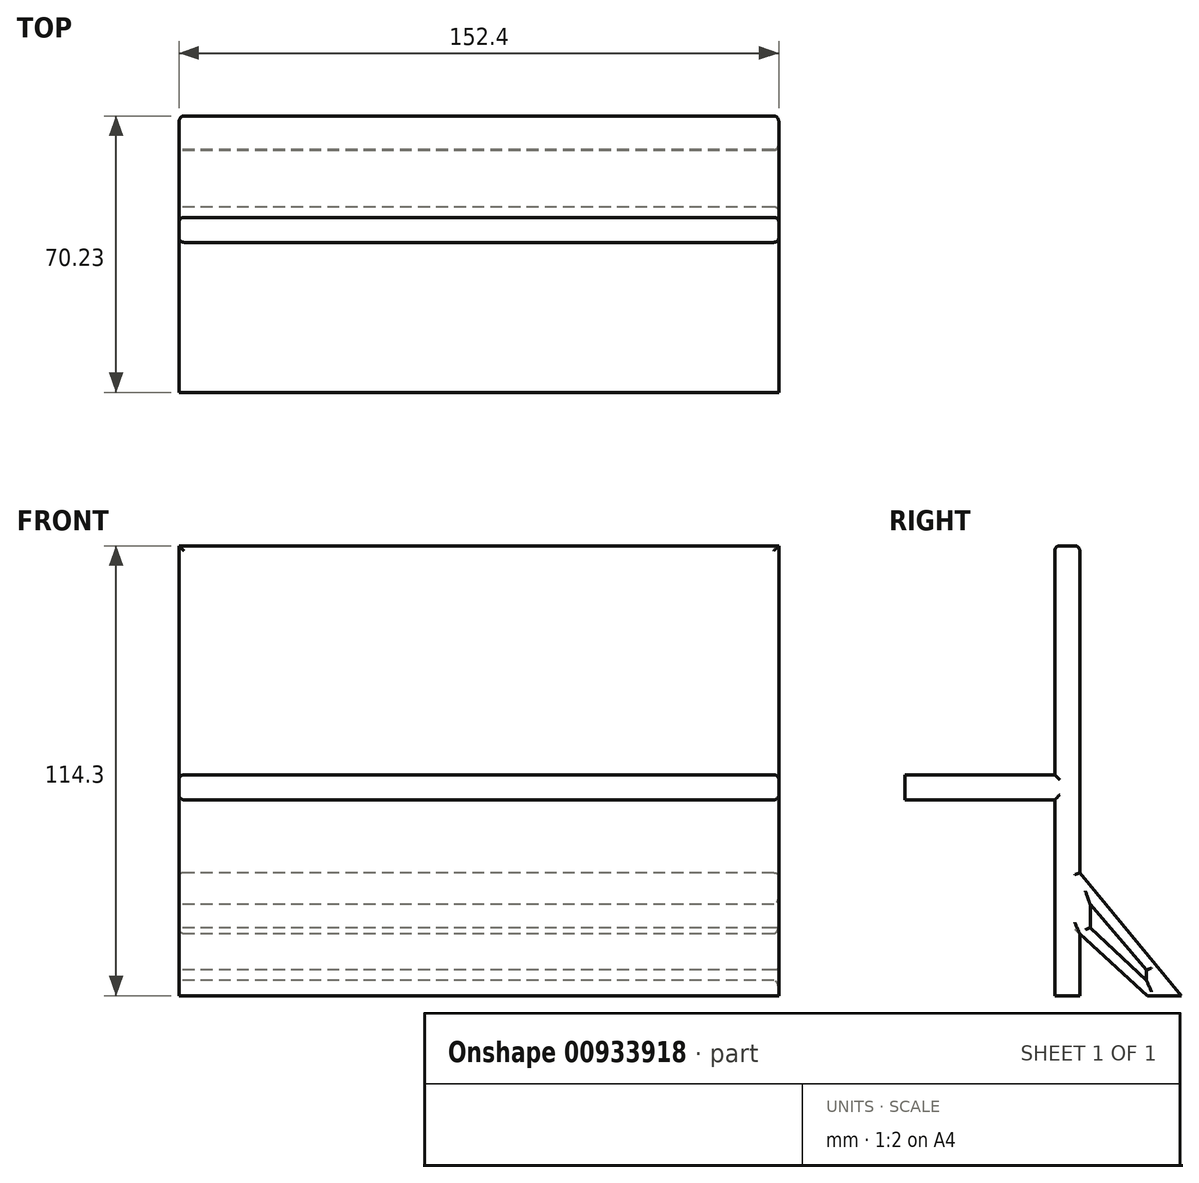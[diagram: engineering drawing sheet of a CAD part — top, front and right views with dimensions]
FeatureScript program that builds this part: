
annotation { "Feature Type Name" : "Feature", "Feature Type Description" : "" }
export const myFeature = defineFeature(function(context is Context, id is Id, definition is map)
    precondition{}
    {
        {
            var Q0;
            Q0=qCreatedBy(makeId("Right.planeOp"),FACE);
            var sketch = newSketch(context, id + "F0", { "sketchPlane" : qUnion([Q0])});
            skLineSegment(sketch, "E0", {"start": v(25.4, -45.43) * mm, "end": v(25.4, 68.87) * mm});
            skLineSegment(sketch, "E1", {"start": v(25.4, 68.87) * mm, "end": v(19.05, 68.87) * mm});
            skLineSegment(sketch, "E2", {"start": v(19.05, 68.87) * mm, "end": v(19.05, -45.43) * mm});
            skLineSegment(sketch, "E3", {"start": v(19.05, -45.43) * mm, "end": v(25.4, -45.43) * mm});
            skLineSegment(sketch, "E4", {"start": v(25.4, -45.43) * mm, "end": v(66.93, -45.43) * mm, "construction": true});
            skLineSegment(sketch, "E5", {"start": v(51.18, -45.43) * mm, "end": v(25.4, -14.25) * mm});
            skLineSegment(sketch, "E6", {"start": v(25.4, -14.25) * mm, "end": v(25.4, -29.7) * mm});
            skLineSegment(sketch, "E7", {"start": v(25.4, -29.7) * mm, "end": v(42.58, -45.43) * mm});
            skLineSegment(sketch, "E8", {"start": v(42.58, -45.43) * mm, "end": v(51.18, -45.43) * mm});
            skLineSegment(sketch, "E9", {"start": v(28.05, -22.21) * mm, "end": v(28.05, -28.15) * mm});
            skLineSegment(sketch, "E10", {"start": v(28.05, -28.15) * mm, "end": v(42.37, -41.55) * mm});
            skLineSegment(sketch, "E11", {"start": v(42.37, -41.55) * mm, "end": v(42.37, -38.9) * mm});
            skLineSegment(sketch, "E12", {"start": v(42.37, -38.9) * mm, "end": v(28.05, -22.21) * mm});
            skSolve(sketch);
        }
        {
            var Q0;
            Q0=qCreatedBy(makeId("Right.planeOp"),FACE);
            var sketch = newSketch(context, id + "F1", { "sketchPlane" : qUnion([Q0])});
            skLineSegment(sketch, "E13.0", {"start": v(19.05, 68.87) * mm, "end": v(19.05, -45.43) * mm});
            skLineSegment(sketch, "E14.0", {"start": v(-19.05, 68.87) * mm, "end": v(-19.05, -45.43) * mm});
            skLineSegment(sketch, "E15", {"start": v(0, -46.47) * mm, "end": v(0, 4.33) * mm, "construction": true});
            skLineSegment(sketch, "E16", {"start": v(19.05, 4.33) * mm, "end": v(-19.05, 4.33) * mm});
            skLineSegment(sketch, "E17", {"start": v(-19.05, 4.33) * mm, "end": v(-19.05, 10.68) * mm});
            skLineSegment(sketch, "E18", {"start": v(-19.05, 10.68) * mm, "end": v(19.05, 10.68) * mm});
            skPoint(sketch, "E18.endSnap0", {"position": v(19.05, 11.72) * mm});
            skLineSegment(sketch, "E19", {"start": v(19.05, 10.68) * mm, "end": v(19.05, 4.33) * mm});
            skSolve(sketch);
        }
        {
            var Q0;
            Q0=makeQuery(id+"F0.imprint","IMPRINT",FACE,{"disambiguationData":[TD([[makeQuery(id+"F0.imprint","IMPRINT",EDGE,{"derivedFrom":sQuery(id+"F0.wireOp",EDGE,"E5")}),1.0]])]});
            var Q1;
            Q1=makeQuery(id+"F0.imprint","IMPRINT",FACE,{"disambiguationData":[TD([[makeQuery(id+"F0.imprint","IMPRINT",EDGE,{"derivedFrom":sQuery(id+"F0.wireOp",EDGE,"E9")}),1.0]])]});
            var Q2;
            {var subQ0=sQuery(id+"F0.wireOp",EDGE,"E1");Q2=makeQuery(id+"F0.imprint","IMPRINT",FACE,{"disambiguationData":[TD([[makeQuery(id+"F0.imprint","IMPRINT",EDGE,{"derivedFrom":subQ0}),1.0]])]});}
            var Q3;
            Q3=makeQuery(id+"F1.imprint","IMPRINT",FACE,{"disambiguationData":[TD([[makeQuery(id+"F1.imprint","IMPRINT",EDGE,{"derivedFrom":sQuery(id+"F1.wireOp",EDGE,"E16")}),-1.0]])]});
            var Q4;
            {var subQ0=sQuery(id+"Fzd2bILkkweZFFx_0.1.F0.wireOp",EDGE,"E1");Q4=makeQuery(id+"Fzd2bILkkweZFFx_0.1.F0.imprint","IMPRINT",FACE,{"disambiguationData":[TD([[makeQuery(id+"Fzd2bILkkweZFFx_0.1.F0.imprint","IMPRINT",EDGE,{"derivedFrom":subQ0}),1.0]])]});}
            var Q5;
            Q5=makeQuery(id+"Fzd2bILkkweZFFx_0.1.F0.imprint","IMPRINT",FACE,{"disambiguationData":[TD([[makeQuery(id+"Fzd2bILkkweZFFx_0.1.F0.imprint","IMPRINT",EDGE,{"derivedFrom":sQuery(id+"Fzd2bILkkweZFFx_0.1.F0.wireOp",EDGE,"E5")}),1.0]])]});
            var Q6;
            Q6=makeQuery(id+"Fzd2bILkkweZFFx_0.1.F0.imprint","IMPRINT",FACE,{"disambiguationData":[TD([[makeQuery(id+"Fzd2bILkkweZFFx_0.1.F0.imprint","IMPRINT",EDGE,{"derivedFrom":sQuery(id+"Fzd2bILkkweZFFx_0.1.F0.wireOp",EDGE,"E9")}),1.0]])]});
            extrude(context, id + "F2", {"entities" : qUnion([Q0, Q1, Q2, Q3, Q4, Q5, Q6]), "depth" : 152.4 * mm, "offsetDistance" : 25.4 * mm});
        }
        {
            var Q0;
            Q0=makeQuery(id+"F0.imprint","IMPRINT",FACE,{"disambiguationData":[TD([[makeQuery(id+"F0.imprint","IMPRINT",EDGE,{"derivedFrom":sQuery(id+"F0.wireOp",EDGE,"E9")}),1.0]])]});
            var Q1;
            Q1=makeQuery(id+"Fzd2bILkkweZFFx_0.1.F0.imprint","IMPRINT",FACE,{"disambiguationData":[TD([[makeQuery(id+"Fzd2bILkkweZFFx_0.1.F0.imprint","IMPRINT",EDGE,{"derivedFrom":sQuery(id+"Fzd2bILkkweZFFx_0.1.F0.wireOp",EDGE,"E9")}),1.0]])]});
            extrude(context, id + "F3", {"entities" : qUnion([Q0, Q1]), "operationType" : NewBodyOperationType.REMOVE, "depth" : 157.48 * mm, "offsetDistance" : 25.4 * mm});
        }
        {
            var Q0;
            Q0=makeQuery(id+"F2.opExtrude","SWEPT_BODY",BODY,{"disambiguationData":[OSD([sQuery(id+"F0.wireOp",EDGE,"E0"),sQuery(id+"F0.wireOp",EDGE,"E1"),sQuery(id+"F0.wireOp",EDGE,"E2"),sQuery(id+"F0.wireOp",EDGE,"E3"),sQuery(id+"F0.wireOp",EDGE,"E5"),sQuery(id+"F0.wireOp",EDGE,"E7"),sQuery(id+"F0.wireOp",EDGE,"E8")])]});
            var Q1;
            Q1=makeQuery(id+"F2.opExtrude","SWEPT_BODY",BODY,{"disambiguationData":[OSD([sQuery(id+"Fzd2bILkkweZFFx_0.1.F0.wireOp",EDGE,"E0"),sQuery(id+"Fzd2bILkkweZFFx_0.1.F0.wireOp",EDGE,"E1"),sQuery(id+"Fzd2bILkkweZFFx_0.1.F0.wireOp",EDGE,"E2"),sQuery(id+"Fzd2bILkkweZFFx_0.1.F0.wireOp",EDGE,"E3"),sQuery(id+"Fzd2bILkkweZFFx_0.1.F0.wireOp",EDGE,"E5"),sQuery(id+"Fzd2bILkkweZFFx_0.1.F0.wireOp",EDGE,"E7"),sQuery(id+"Fzd2bILkkweZFFx_0.1.F0.wireOp",EDGE,"E8")])]});
            var Q2;
            Q2=makeQuery(id+"F2.opExtrude","SWEPT_BODY",BODY,{"disambiguationData":[OSD([sQuery(id+"F1.wireOp",EDGE,"E16"),sQuery(id+"F1.wireOp",EDGE,"E17"),sQuery(id+"F1.wireOp",EDGE,"E18"),sQuery(id+"F1.wireOp",EDGE,"E19")])]});
            booleanBodies(context, id + "F4", {"operationType" : BooleanOperationType.UNION, "tools" : qUnion([Q0, Q1, Q2])});
        }
        {
            var Q0;
            Q0=makeQuery(id+"F2.opExtrude","SWEPT_EDGE",EDGE,{"disambiguationData":[OSD([sQuery(id+"Fzd2bILkkweZFFx_0.1.F0.wireOp",EDGE,"E1"),sQuery(id+"Fzd2bILkkweZFFx_0.1.F0.wireOp",EDGE,"E2")])]});
            var Q1;
            Q1=makeQuery(id+"F2.opExtrude","SWEPT_EDGE",EDGE,{"disambiguationData":[OSD([sQuery(id+"F0.wireOp",EDGE,"E1"),sQuery(id+"F0.wireOp",EDGE,"E2")])]});
            var Q2;
            {var subQ0=sQuery(id+"Fzd2bILkkweZFFx_0.1.F0.wireOp",EDGE,"E2");var subQ1=sQuery(id+"Fzd2bILkkweZFFx_0.1.F0.wireOp",EDGE,"E1");Q2=makeQuery(id+"F4.opBoolean","SPLIT",EDGE,{"disambiguationData":[TD([makeQuery(id+"F2.opExtrude","SWEPT_FACE",FACE,{"disambiguationData":[OSD([subQ1])]})])],"derivedFrom":makeQuery(id+"F2.opExtrude","CAP_EDGE",EDGE,{"disambiguationData":[OSD([subQ0])],"isStart":false})});}
            var Q3;
            {var subQ0=sQuery(id+"F0.wireOp",EDGE,"E2");var subQ1=sQuery(id+"F0.wireOp",EDGE,"E1");Q3=makeQuery(id+"F4.opBoolean","SPLIT",EDGE,{"disambiguationData":[TD([makeQuery(id+"F2.opExtrude","SWEPT_FACE",FACE,{"disambiguationData":[OSD([subQ1])]})])],"derivedFrom":makeQuery(id+"F2.opExtrude","CAP_EDGE",EDGE,{"disambiguationData":[OSD([subQ0])],"isStart":false})});}
            var Q4;
            {var subQ0=sQuery(id+"Fzd2bILkkweZFFx_0.1.F0.wireOp",EDGE,"E3");var subQ1=sQuery(id+"Fzd2bILkkweZFFx_0.1.F0.wireOp",EDGE,"E2");Q4=makeQuery(id+"F4.opBoolean","SPLIT",EDGE,{"disambiguationData":[TD([makeQuery(id+"F2.opExtrude","SWEPT_FACE",FACE,{"disambiguationData":[OSD([subQ0])]})])],"derivedFrom":makeQuery(id+"F2.opExtrude","CAP_EDGE",EDGE,{"disambiguationData":[OSD([subQ1])],"isStart":false})});}
            var Q5;
            {var subQ0=sQuery(id+"F0.wireOp",EDGE,"E3");var subQ1=sQuery(id+"F0.wireOp",EDGE,"E2");Q5=makeQuery(id+"F4.opBoolean","SPLIT",EDGE,{"disambiguationData":[TD([makeQuery(id+"F2.opExtrude","SWEPT_FACE",FACE,{"disambiguationData":[OSD([subQ0])]})])],"derivedFrom":makeQuery(id+"F2.opExtrude","CAP_EDGE",EDGE,{"disambiguationData":[OSD([subQ1])],"isStart":false})});}
            var Q6;
            Q6=makeQuery(id+"F2.opExtrude","CAP_EDGE",EDGE,{"disambiguationData":[OSD([sQuery(id+"F1.wireOp",EDGE,"E16")])],"isStart":false});
            var Q7;
            Q7=makeQuery(id+"F2.opExtrude","CAP_EDGE",EDGE,{"disambiguationData":[OSD([sQuery(id+"F1.wireOp",EDGE,"E18")])],"isStart":false});
            var Q8;
            Q8=makeQuery(id+"F2.opExtrude","CAP_EDGE",EDGE,{"disambiguationData":[OSD([sQuery(id+"F1.wireOp",EDGE,"E18")])],"isStart":true});
            var Q9;
            Q9=makeQuery(id+"F2.opExtrude","CAP_EDGE",EDGE,{"disambiguationData":[OSD([sQuery(id+"F1.wireOp",EDGE,"E16")])],"isStart":true});
            var Q10;
            {var subQ0=sQuery(id+"F0.wireOp",EDGE,"E2");var subQ1=sQuery(id+"F0.wireOp",EDGE,"E1");Q10=makeQuery(id+"F4.opBoolean","SPLIT",EDGE,{"disambiguationData":[TD([makeQuery(id+"F2.opExtrude","SWEPT_FACE",FACE,{"disambiguationData":[OSD([subQ1])]})])],"derivedFrom":makeQuery(id+"F2.opExtrude","CAP_EDGE",EDGE,{"disambiguationData":[OSD([subQ0])],"isStart":true})});}
            var Q11;
            {var subQ0=sQuery(id+"F0.wireOp",EDGE,"E2");var subQ1=sQuery(id+"F0.wireOp",EDGE,"E3");Q11=makeQuery(id+"F4.opBoolean","SPLIT",EDGE,{"disambiguationData":[TD([makeQuery(id+"F2.opExtrude","SWEPT_FACE",FACE,{"disambiguationData":[OSD([subQ1])]})])],"derivedFrom":makeQuery(id+"F2.opExtrude","CAP_EDGE",EDGE,{"disambiguationData":[OSD([subQ0])],"isStart":true})});}
            var Q12;
            {var subQ0=sQuery(id+"Fzd2bILkkweZFFx_0.1.F0.wireOp",EDGE,"E2");var subQ1=sQuery(id+"Fzd2bILkkweZFFx_0.1.F0.wireOp",EDGE,"E3");Q12=makeQuery(id+"F4.opBoolean","SPLIT",EDGE,{"disambiguationData":[TD([makeQuery(id+"F2.opExtrude","SWEPT_FACE",FACE,{"disambiguationData":[OSD([subQ1])]})])],"derivedFrom":makeQuery(id+"F2.opExtrude","CAP_EDGE",EDGE,{"disambiguationData":[OSD([subQ0])],"isStart":true})});}
            var Q13;
            {var subQ0=sQuery(id+"Fzd2bILkkweZFFx_0.1.F0.wireOp",EDGE,"E2");var subQ1=sQuery(id+"Fzd2bILkkweZFFx_0.1.F0.wireOp",EDGE,"E1");Q13=makeQuery(id+"F4.opBoolean","SPLIT",EDGE,{"disambiguationData":[TD([makeQuery(id+"F2.opExtrude","SWEPT_FACE",FACE,{"disambiguationData":[OSD([subQ1])]})])],"derivedFrom":makeQuery(id+"F2.opExtrude","CAP_EDGE",EDGE,{"disambiguationData":[OSD([subQ0])],"isStart":true})});}
            var Q14;
            Q14=makeQuery(id+"F2.opExtrude","SWEPT_EDGE",EDGE,{"disambiguationData":[OSD([sQuery(id+"Fzd2bILkkweZFFx_0.1.F0.wireOp",EDGE,"E0"),sQuery(id+"Fzd2bILkkweZFFx_0.1.F0.wireOp",EDGE,"E1")])]});
            var Q15;
            {var subQ0=sQuery(id+"Fzd2bILkkweZFFx_0.1.F0.wireOp",EDGE,"E0");Q15=makeQuery(id+"F2.opExtrude","CAP_EDGE",EDGE,{"disambiguationData":[OSD([subQ0]),TDD([makeQuery(id+"Fzd2bILkkweZFFx_0.1.F0.imprint","IMPRINT",EDGE,{"disambiguationData":[TD([[makeQuery(id+"Fzd2bILkkweZFFx_0.1.F0.imprint","INTERSECT",VERTEX,{"derivedFrom":[subQ0,sQuery(id+"Fzd2bILkkweZFFx_0.1.F0.wireOp",EDGE,"E1")]}),1.0]])],"derivedFrom":subQ0})])],"isStart":false});}
            var Q16;
            {var subQ0=sQuery(id+"Fzd2bILkkweZFFx_0.1.F0.wireOp",EDGE,"E0");Q16=makeQuery(id+"F2.opExtrude","CAP_EDGE",EDGE,{"disambiguationData":[OSD([subQ0]),TDD([makeQuery(id+"Fzd2bILkkweZFFx_0.1.F0.imprint","IMPRINT",EDGE,{"disambiguationData":[TD([[makeQuery(id+"Fzd2bILkkweZFFx_0.1.F0.imprint","INTERSECT",VERTEX,{"derivedFrom":[subQ0,sQuery(id+"Fzd2bILkkweZFFx_0.1.F0.wireOp",EDGE,"E1")]}),1.0]])],"derivedFrom":subQ0})])],"isStart":true});}
            var Q17;
            {var subQ0=sQuery(id+"F0.wireOp",EDGE,"E0");Q17=makeQuery(id+"F2.opExtrude","CAP_EDGE",EDGE,{"disambiguationData":[OSD([subQ0]),TDD([makeQuery(id+"F0.imprint","IMPRINT",EDGE,{"disambiguationData":[TD([[makeQuery(id+"F0.imprint","INTERSECT",VERTEX,{"derivedFrom":[subQ0,sQuery(id+"F0.wireOp",EDGE,"E1")]}),1.0]])],"derivedFrom":subQ0})])],"isStart":true});}
            var Q18;
            Q18=makeQuery(id+"F2.opExtrude","SWEPT_EDGE",EDGE,{"disambiguationData":[OSD([sQuery(id+"F0.wireOp",EDGE,"E0"),sQuery(id+"F0.wireOp",EDGE,"E1")])]});
            var Q19;
            {var subQ0=sQuery(id+"F0.wireOp",EDGE,"E0");Q19=makeQuery(id+"F2.opExtrude","CAP_EDGE",EDGE,{"disambiguationData":[OSD([subQ0]),TDD([makeQuery(id+"F0.imprint","IMPRINT",EDGE,{"disambiguationData":[TD([[makeQuery(id+"F0.imprint","INTERSECT",VERTEX,{"derivedFrom":[subQ0,sQuery(id+"F0.wireOp",EDGE,"E1")]}),1.0]])],"derivedFrom":subQ0})])],"isStart":false});}
            fillet(context, id + "F5", {"entities" : qUnion([Q0, Q1, Q2, Q3, Q4, Q5, Q6, Q7, Q8, Q9, Q10, Q11, Q12, Q13, Q14, Q15, Q16, Q17, Q18, Q19]), "radius" : 1.27 * mm, "tangentPropagation" : true, "allowEdgeOverflow" : false});
        }
        {
            var Q0;
            Q0=makeQuery(id+"F3.boolean.opBoolean","INTERSECT",EDGE,{"derivedFrom":[makeQuery(id+"F2.opExtrude","CAP_FACE",FACE,{"disambiguationData":[OSD([sQuery(id+"Fzd2bILkkweZFFx_0.1.F0.wireOp",EDGE,"E0"),sQuery(id+"Fzd2bILkkweZFFx_0.1.F0.wireOp",EDGE,"E1"),sQuery(id+"Fzd2bILkkweZFFx_0.1.F0.wireOp",EDGE,"E2"),sQuery(id+"Fzd2bILkkweZFFx_0.1.F0.wireOp",EDGE,"E3"),sQuery(id+"Fzd2bILkkweZFFx_0.1.F0.wireOp",EDGE,"E5"),sQuery(id+"Fzd2bILkkweZFFx_0.1.F0.wireOp",EDGE,"E7"),sQuery(id+"Fzd2bILkkweZFFx_0.1.F0.wireOp",EDGE,"E8")])],"isStart":false}),makeQuery(id+"F3.opExtrude","SWEPT_FACE",FACE,{"disambiguationData":[OSD([sQuery(id+"Fzd2bILkkweZFFx_0.1.F0.wireOp",EDGE,"E12")])]})]});
            var Q1;
            Q1=makeQuery(id+"F3.boolean.opBoolean","INTERSECT",EDGE,{"derivedFrom":[makeQuery(id+"F2.opExtrude","CAP_FACE",FACE,{"disambiguationData":[OSD([sQuery(id+"Fzd2bILkkweZFFx_0.1.F0.wireOp",EDGE,"E0"),sQuery(id+"Fzd2bILkkweZFFx_0.1.F0.wireOp",EDGE,"E1"),sQuery(id+"Fzd2bILkkweZFFx_0.1.F0.wireOp",EDGE,"E2"),sQuery(id+"Fzd2bILkkweZFFx_0.1.F0.wireOp",EDGE,"E3"),sQuery(id+"Fzd2bILkkweZFFx_0.1.F0.wireOp",EDGE,"E5"),sQuery(id+"Fzd2bILkkweZFFx_0.1.F0.wireOp",EDGE,"E7"),sQuery(id+"Fzd2bILkkweZFFx_0.1.F0.wireOp",EDGE,"E8")])],"isStart":false}),makeQuery(id+"F3.opExtrude","SWEPT_FACE",FACE,{"disambiguationData":[OSD([sQuery(id+"Fzd2bILkkweZFFx_0.1.F0.wireOp",EDGE,"E10")])]})]});
            var Q2;
            Q2=makeQuery(id+"F3.boolean.opBoolean","INTERSECT",EDGE,{"derivedFrom":[makeQuery(id+"F2.opExtrude","CAP_FACE",FACE,{"disambiguationData":[OSD([sQuery(id+"Fzd2bILkkweZFFx_0.1.F0.wireOp",EDGE,"E0"),sQuery(id+"Fzd2bILkkweZFFx_0.1.F0.wireOp",EDGE,"E1"),sQuery(id+"Fzd2bILkkweZFFx_0.1.F0.wireOp",EDGE,"E2"),sQuery(id+"Fzd2bILkkweZFFx_0.1.F0.wireOp",EDGE,"E3"),sQuery(id+"Fzd2bILkkweZFFx_0.1.F0.wireOp",EDGE,"E5"),sQuery(id+"Fzd2bILkkweZFFx_0.1.F0.wireOp",EDGE,"E7"),sQuery(id+"Fzd2bILkkweZFFx_0.1.F0.wireOp",EDGE,"E8")])],"isStart":false}),makeQuery(id+"F3.opExtrude","SWEPT_FACE",FACE,{"disambiguationData":[OSD([sQuery(id+"Fzd2bILkkweZFFx_0.1.F0.wireOp",EDGE,"E9")])]})]});
            var Q3;
            Q3=makeQuery(id+"F3.boolean.opBoolean","INTERSECT",EDGE,{"derivedFrom":[makeQuery(id+"F2.opExtrude","CAP_FACE",FACE,{"disambiguationData":[OSD([sQuery(id+"Fzd2bILkkweZFFx_0.1.F0.wireOp",EDGE,"E0"),sQuery(id+"Fzd2bILkkweZFFx_0.1.F0.wireOp",EDGE,"E1"),sQuery(id+"Fzd2bILkkweZFFx_0.1.F0.wireOp",EDGE,"E2"),sQuery(id+"Fzd2bILkkweZFFx_0.1.F0.wireOp",EDGE,"E3"),sQuery(id+"Fzd2bILkkweZFFx_0.1.F0.wireOp",EDGE,"E5"),sQuery(id+"Fzd2bILkkweZFFx_0.1.F0.wireOp",EDGE,"E7"),sQuery(id+"Fzd2bILkkweZFFx_0.1.F0.wireOp",EDGE,"E8")])],"isStart":false}),makeQuery(id+"F3.opExtrude","SWEPT_FACE",FACE,{"disambiguationData":[OSD([sQuery(id+"Fzd2bILkkweZFFx_0.1.F0.wireOp",EDGE,"E11")])]})]});
            var Q4;
            Q4=makeQuery(id+"F3.boolean.opBoolean","INTERSECT",EDGE,{"derivedFrom":[makeQuery(id+"F2.opExtrude","CAP_FACE",FACE,{"disambiguationData":[OSD([sQuery(id+"F0.wireOp",EDGE,"E0"),sQuery(id+"F0.wireOp",EDGE,"E1"),sQuery(id+"F0.wireOp",EDGE,"E2"),sQuery(id+"F0.wireOp",EDGE,"E3"),sQuery(id+"F0.wireOp",EDGE,"E5"),sQuery(id+"F0.wireOp",EDGE,"E7"),sQuery(id+"F0.wireOp",EDGE,"E8")])],"isStart":false}),makeQuery(id+"F3.opExtrude","SWEPT_FACE",FACE,{"disambiguationData":[OSD([sQuery(id+"F0.wireOp",EDGE,"E10")])]})]});
            var Q5;
            Q5=makeQuery(id+"F3.boolean.opBoolean","INTERSECT",EDGE,{"derivedFrom":[makeQuery(id+"F2.opExtrude","CAP_FACE",FACE,{"disambiguationData":[OSD([sQuery(id+"F0.wireOp",EDGE,"E0"),sQuery(id+"F0.wireOp",EDGE,"E1"),sQuery(id+"F0.wireOp",EDGE,"E2"),sQuery(id+"F0.wireOp",EDGE,"E3"),sQuery(id+"F0.wireOp",EDGE,"E5"),sQuery(id+"F0.wireOp",EDGE,"E7"),sQuery(id+"F0.wireOp",EDGE,"E8")])],"isStart":false}),makeQuery(id+"F3.opExtrude","SWEPT_FACE",FACE,{"disambiguationData":[OSD([sQuery(id+"F0.wireOp",EDGE,"E12")])]})]});
            var Q6;
            Q6=makeQuery(id+"F3.boolean.opBoolean","INTERSECT",EDGE,{"derivedFrom":[makeQuery(id+"F2.opExtrude","CAP_FACE",FACE,{"disambiguationData":[OSD([sQuery(id+"F0.wireOp",EDGE,"E0"),sQuery(id+"F0.wireOp",EDGE,"E1"),sQuery(id+"F0.wireOp",EDGE,"E2"),sQuery(id+"F0.wireOp",EDGE,"E3"),sQuery(id+"F0.wireOp",EDGE,"E5"),sQuery(id+"F0.wireOp",EDGE,"E7"),sQuery(id+"F0.wireOp",EDGE,"E8")])],"isStart":false}),makeQuery(id+"F3.opExtrude","SWEPT_FACE",FACE,{"disambiguationData":[OSD([sQuery(id+"F0.wireOp",EDGE,"E9")])]})]});
            var Q7;
            Q7=makeQuery(id+"F3.boolean.opBoolean","INTERSECT",EDGE,{"derivedFrom":[makeQuery(id+"F2.opExtrude","CAP_FACE",FACE,{"disambiguationData":[OSD([sQuery(id+"F0.wireOp",EDGE,"E0"),sQuery(id+"F0.wireOp",EDGE,"E1"),sQuery(id+"F0.wireOp",EDGE,"E2"),sQuery(id+"F0.wireOp",EDGE,"E3"),sQuery(id+"F0.wireOp",EDGE,"E5"),sQuery(id+"F0.wireOp",EDGE,"E7"),sQuery(id+"F0.wireOp",EDGE,"E8")])],"isStart":false}),makeQuery(id+"F3.opExtrude","SWEPT_FACE",FACE,{"disambiguationData":[OSD([sQuery(id+"F0.wireOp",EDGE,"E11")])]})]});
            var Q8;
            Q8=makeQuery(id+"F3.boolean.opBoolean","COPY",EDGE,{"derivedFrom":makeQuery(id+"F3.opExtrude","CAP_EDGE",EDGE,{"disambiguationData":[OSD([sQuery(id+"F0.wireOp",EDGE,"E12")])],"isStart":true})});
            var Q9;
            Q9=makeQuery(id+"F3.boolean.opBoolean","COPY",EDGE,{"derivedFrom":makeQuery(id+"F3.opExtrude","CAP_EDGE",EDGE,{"disambiguationData":[OSD([sQuery(id+"F0.wireOp",EDGE,"E11")])],"isStart":true})});
            var Q10;
            Q10=makeQuery(id+"F3.boolean.opBoolean","COPY",EDGE,{"derivedFrom":makeQuery(id+"F3.opExtrude","CAP_EDGE",EDGE,{"disambiguationData":[OSD([sQuery(id+"F0.wireOp",EDGE,"E10")])],"isStart":true})});
            var Q11;
            Q11=makeQuery(id+"F3.boolean.opBoolean","COPY",EDGE,{"derivedFrom":makeQuery(id+"F3.opExtrude","CAP_EDGE",EDGE,{"disambiguationData":[OSD([sQuery(id+"F0.wireOp",EDGE,"E9")])],"isStart":true})});
            var Q12;
            Q12=makeQuery(id+"F3.boolean.opBoolean","COPY",EDGE,{"derivedFrom":makeQuery(id+"F3.opExtrude","CAP_EDGE",EDGE,{"disambiguationData":[OSD([sQuery(id+"Fzd2bILkkweZFFx_0.1.F0.wireOp",EDGE,"E12")])],"isStart":true})});
            var Q13;
            Q13=makeQuery(id+"F3.boolean.opBoolean","COPY",EDGE,{"derivedFrom":makeQuery(id+"F3.opExtrude","CAP_EDGE",EDGE,{"disambiguationData":[OSD([sQuery(id+"Fzd2bILkkweZFFx_0.1.F0.wireOp",EDGE,"E10")])],"isStart":true})});
            var Q14;
            Q14=makeQuery(id+"F3.boolean.opBoolean","COPY",EDGE,{"derivedFrom":makeQuery(id+"F3.opExtrude","CAP_EDGE",EDGE,{"disambiguationData":[OSD([sQuery(id+"Fzd2bILkkweZFFx_0.1.F0.wireOp",EDGE,"E9")])],"isStart":true})});
            var Q15;
            Q15=makeQuery(id+"F3.boolean.opBoolean","COPY",EDGE,{"derivedFrom":makeQuery(id+"F3.opExtrude","CAP_EDGE",EDGE,{"disambiguationData":[OSD([sQuery(id+"Fzd2bILkkweZFFx_0.1.F0.wireOp",EDGE,"E11")])],"isStart":true})});
            fillet(context, id + "F6", {"entities" : qUnion([Q0, Q1, Q2, Q3, Q4, Q5, Q6, Q7, Q8, Q9, Q10, Q11, Q12, Q13, Q14, Q15]), "radius" : 1.27 * mm, "tangentPropagation" : true, "allowEdgeOverflow" : false});
        }
        {
            var Q0;
            Q0=makeQuery(id+"F2.opExtrude","CAP_EDGE",EDGE,{"disambiguationData":[OSD([sQuery(id+"F0.wireOp",EDGE,"E5")])],"isStart":true});
            var Q1;
            Q1=makeQuery(id+"F2.opExtrude","CAP_EDGE",EDGE,{"disambiguationData":[OSD([sQuery(id+"F0.wireOp",EDGE,"E5")])],"isStart":false});
            var Q2;
            Q2=makeQuery(id+"F2.opExtrude","CAP_EDGE",EDGE,{"disambiguationData":[OSD([sQuery(id+"F0.wireOp",EDGE,"E7")])],"isStart":false});
            var Q3;
            {var subQ0=sQuery(id+"F0.wireOp",EDGE,"E0");Q3=makeQuery(id+"F2.opExtrude","CAP_EDGE",EDGE,{"disambiguationData":[OSD([subQ0]),TDD([makeQuery(id+"F0.imprint","IMPRINT",EDGE,{"disambiguationData":[TD([[makeQuery(id+"F0.imprint","INTERSECT",VERTEX,{"derivedFrom":[subQ0,sQuery(id+"F0.wireOp",EDGE,"E3")]}),-1.0]])],"derivedFrom":subQ0})])],"isStart":false});}
            var Q4;
            {var subQ0=sQuery(id+"F0.wireOp",EDGE,"E0");Q4=makeQuery(id+"F2.opExtrude","CAP_EDGE",EDGE,{"disambiguationData":[OSD([subQ0]),TDD([makeQuery(id+"F0.imprint","IMPRINT",EDGE,{"disambiguationData":[TD([[makeQuery(id+"F0.imprint","INTERSECT",VERTEX,{"derivedFrom":[subQ0,sQuery(id+"F0.wireOp",EDGE,"E3")]}),-1.0]])],"derivedFrom":subQ0})])],"isStart":true});}
            var Q5;
            Q5=makeQuery(id+"F2.opExtrude","CAP_EDGE",EDGE,{"disambiguationData":[OSD([sQuery(id+"Fzd2bILkkweZFFx_0.1.F0.wireOp",EDGE,"E5")])],"isStart":true});
            var Q6;
            Q6=makeQuery(id+"F2.opExtrude","CAP_EDGE",EDGE,{"disambiguationData":[OSD([sQuery(id+"Fzd2bILkkweZFFx_0.1.F0.wireOp",EDGE,"E7")])],"isStart":true});
            var Q7;
            {var subQ0=sQuery(id+"Fzd2bILkkweZFFx_0.1.F0.wireOp",EDGE,"E0");Q7=makeQuery(id+"F2.opExtrude","CAP_EDGE",EDGE,{"disambiguationData":[OSD([subQ0]),TDD([makeQuery(id+"Fzd2bILkkweZFFx_0.1.F0.imprint","IMPRINT",EDGE,{"disambiguationData":[TD([[makeQuery(id+"Fzd2bILkkweZFFx_0.1.F0.imprint","INTERSECT",VERTEX,{"derivedFrom":[subQ0,sQuery(id+"Fzd2bILkkweZFFx_0.1.F0.wireOp",EDGE,"E3")]}),-1.0]])],"derivedFrom":subQ0})])],"isStart":true});}
            var Q8;
            Q8=makeQuery(id+"F2.opExtrude","CAP_EDGE",EDGE,{"disambiguationData":[OSD([sQuery(id+"Fzd2bILkkweZFFx_0.1.F0.wireOp",EDGE,"E5")])],"isStart":false});
            var Q9;
            Q9=makeQuery(id+"F2.opExtrude","CAP_EDGE",EDGE,{"disambiguationData":[OSD([sQuery(id+"Fzd2bILkkweZFFx_0.1.F0.wireOp",EDGE,"E7")])],"isStart":false});
            var Q10;
            {var subQ0=sQuery(id+"Fzd2bILkkweZFFx_0.1.F0.wireOp",EDGE,"E0");Q10=makeQuery(id+"F2.opExtrude","CAP_EDGE",EDGE,{"disambiguationData":[OSD([subQ0]),TDD([makeQuery(id+"Fzd2bILkkweZFFx_0.1.F0.imprint","IMPRINT",EDGE,{"disambiguationData":[TD([[makeQuery(id+"Fzd2bILkkweZFFx_0.1.F0.imprint","INTERSECT",VERTEX,{"derivedFrom":[subQ0,sQuery(id+"Fzd2bILkkweZFFx_0.1.F0.wireOp",EDGE,"E3")]}),-1.0]])],"derivedFrom":subQ0})])],"isStart":false});}
            fillet(context, id + "F7", {"entities" : qUnion([Q0, Q1, Q2, Q3, Q4, Q5, Q6, Q7, Q8, Q9, Q10]), "radius" : 1.27 * mm, "tangentPropagation" : true, "allowEdgeOverflow" : false});
        }
    });
